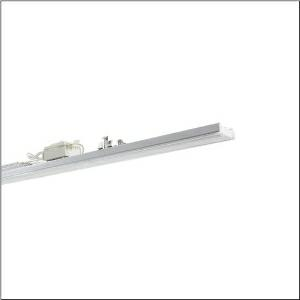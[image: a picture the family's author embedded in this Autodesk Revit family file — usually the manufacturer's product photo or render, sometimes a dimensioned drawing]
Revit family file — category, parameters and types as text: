
# Revit family: licross_r__21_recessed_mo_52tl1edv4e5g_66bd
name_source: partatom
category: Lighting Fixtures
units: mm (PartAtom-declared; Revit-internal decimal feet)

## family parameters
Cut with Voids When Loaded = No
Host = Face
Light Source = No
Part Type = Normal
Room Calculation Point = No
Round Connector Dimension = Use Diameter
Shared = No

## types (1)
- --- (1 x LED, 14910 lm, 85.3 W, 4000K)
    Apparent Load = 85 VA
    CIE Flux Codes = 85 95 99 100 100
    Color Rendering = 80
    Color Temperature = 4000K
    Default Elevation = 1800 mm
    Description = Licross® 21 Recessed MO, luminaire insert, of sheet steel, galvanised, coil coated, white, length: 2.250mm, width: 66mm, height: 67mm, LED rated luminous flux: 14.910lm, light colour: 840, control gear: DALI 2, with plug, 5-pole, with phase selection, mains connection: 220..240V, AC, 50/60Hz, rated input power: 85W, halogen-free wiring, primary light control with lens, of plastic, primary optical cover: cover, of PMMA, light emission: direct distribution, primary light characteristic: symmetric, protection rating (complete): IP40, insulation class (complete): insulation class I (protective earthing), certification: CE, ENEC, VDE, UKCA, protection symbol: D if used in an environment without relevant dust loads with corresponding accessories, impact resistance: IK06, permissible ambient temperature for indoor applications: -25..+35°C, corresponds to IFS (International Featured Standards) requirements for safety and quality in the food industry, reducing of maximum allowable ambient temperature of 5°C with ceiling mounting, LABS conformity tested according to VDMA 24364:2018-05, packaging unit: 1 piece
    Height = 58 mm
    Lamp = 1 x LED
    Lamp Light Flux = 14910 lm
    Lamp Power = 85.3 W
    Lamp count = 1
    Length = 2250 mm
    Luminous efficacy = 175 lm/W
    Manufacturer = Siteco
    ModVariant = No
    Model = 52TL1EDV4E5G
    Mounting Place = Ceiling
    Mounting Type = Pendant
    Number of Poles = 1
    OnlyDefault = Yes
    Power Factor = 1
    Product Name = Licross® 21 Recessed MO
    Product group = luminaire insert
    ProductGroupID = 902
    Protection Class = Protection class I
    Protection Degree = IP 40
    RLX_Detail_Level = 1
    RLX_Emergency_Light_Flux = 0 lm
    RLX_Emergency_Type = 0
    RLX_Emergency_Type_DB = No
    RlxData = <blob elided: 29933 chars, md5=3de3ae33>
    Socket = socket
    Standby Power = 0 W
    System Light Flux = 14910 lm
    System Power = 85 W
    Type Comments = factory setting: luminous flux: 100 % | dim-lin: 254 | 390 mA
    Type Image = l_1296930.jpg
    URL = http://relux.com
    VarID = @adj_125590
    Voltage = 0 V
    Weight = 0.00 kg
    Width = 66 mm

## geometry (parser evidence)
native form markers: Blend x4, Sweep x10
no freeform markers — native parametric forms only
